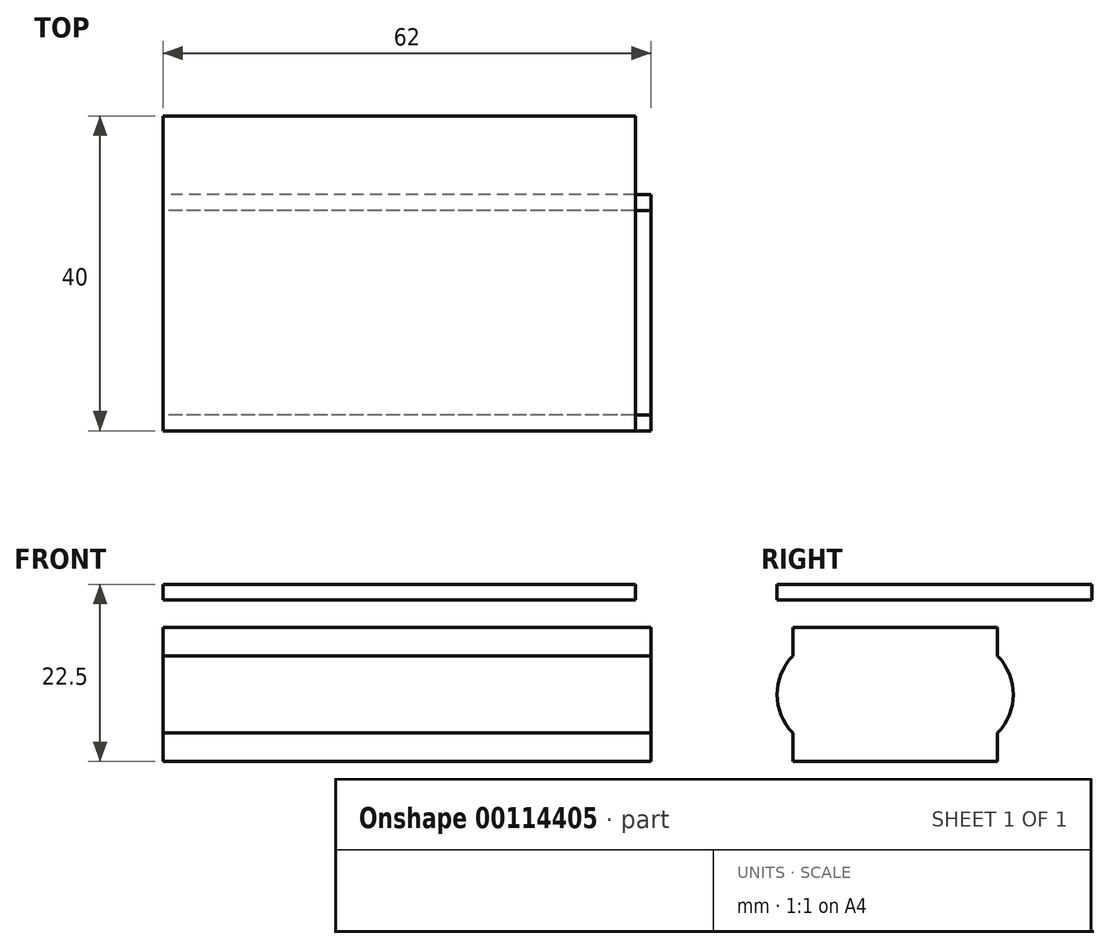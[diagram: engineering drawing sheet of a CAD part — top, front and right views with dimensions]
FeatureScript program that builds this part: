
annotation { "Feature Type Name" : "Feature", "Feature Type Description" : "" }
export const myFeature = defineFeature(function(context is Context, id is Id, definition is map)
    precondition{}
    {
        {
            assignVariable(context, id + "F0", {"name" : "pcb_z", "anyValue" : 2});
        }
        {
            var Q0;
            Q0=qCreatedBy(makeId("Top.planeOp"),FACE);
            var sketch = newSketch(context, id + "F1", { "sketchPlane" : qUnion([Q0])});
            skLineSegment(sketch, "E0.bottom", {"start": v(30, -20) * mm, "end": v(-30, -20) * mm});
            skLineSegment(sketch, "E0.top", {"start": v(30, 20) * mm, "end": v(-30, 20) * mm});
            skLineSegment(sketch, "E0.left", {"start": v(30, -20) * mm, "end": v(30, 20) * mm});
            skLineSegment(sketch, "E0.right", {"start": v(-30, -20) * mm, "end": v(-30, 20) * mm});
            skPoint(sketch, "E0.middle", {"position": v(0, 0) * mm});
            skSolve(sketch);
        }
        {
            var Q0;
            Q0=makeQuery(id+"F1.imprint","IMPRINT",FACE,{"disambiguationData":[TD([[makeQuery(id+"F1.imprint","IMPRINT",EDGE,{"derivedFrom":sQuery(id+"F1.wireOp",EDGE,"E0.bottom")}),-1.0]])]});
            extrude(context, id + "F2", {"entities" : qUnion([Q0]), "depth" : (getVariable(context, 'pcb_z')) * mm});
        }
        {
            var Q0;
            Q0=makeQuery(id+"F2.opExtrude","SWEPT_FACE",FACE,{"disambiguationData":[OSD([sQuery(id+"F1.wireOp",EDGE,"E0.right")])]});
            var sketch = newSketch(context, id + "F3", { "sketchPlane" : qUnion([Q0])});
            skArc(sketch, "E1", {"start": v(-8, -7.1) * mm, "mid": v(-10, -12) * mm, "end": v(-8, -16.9) * mm});
            skArc(sketch, "E2", {"start": v(18, -16.9) * mm, "mid": v(20, -12) * mm, "end": v(18, -7.1) * mm});
            skLineSegment(sketch, "E3.bottom", {"start": v(18, -3.5) * mm, "end": v(-8, -3.5) * mm});
            skLineSegment(sketch, "E3.top", {"start": v(18, -20.5) * mm, "end": v(-8, -20.5) * mm});
            skLineSegment(sketch, "E3.left", {"start": v(18, -3.5) * mm, "end": v(18, -7.1) * mm});
            skLineSegment(sketch, "E3.right", {"start": v(-8, -3.5) * mm, "end": v(-8, -7.1) * mm});
            skPoint(sketch, "E3.middle", {"position": v(5, -12) * mm});
            skLineSegment(sketch, "E4", {"start": v(-3, -12) * mm, "end": v(13, -12) * mm, "construction": true});
            skLineSegment(sketch, "E5.trimOffspring", {"start": v(-8, -16.9) * mm, "end": v(-8, -20.5) * mm});
            skLineSegment(sketch, "E6.trimOffspring", {"start": v(18, -16.9) * mm, "end": v(18, -20.5) * mm});
            skLineSegment(sketch, "E7", {"start": v(20, 0) * mm, "end": v(20, -22) * mm, "construction": true});
            skSolve(sketch);
        }
        {
            var Q0;
            Q0=makeQuery(id+"F3.imprint","IMPRINT",FACE,{"disambiguationData":[TD([[makeQuery(id+"F3.imprint","IMPRINT",EDGE,{"derivedFrom":sQuery(id+"F3.wireOp",EDGE,"E1")}),1.0]])]});
            extrude(context, id + "F4", {"entities" : qUnion([Q0]), "oppositeDirection" : true, "depth" : 62 * mm});
        }
    });
